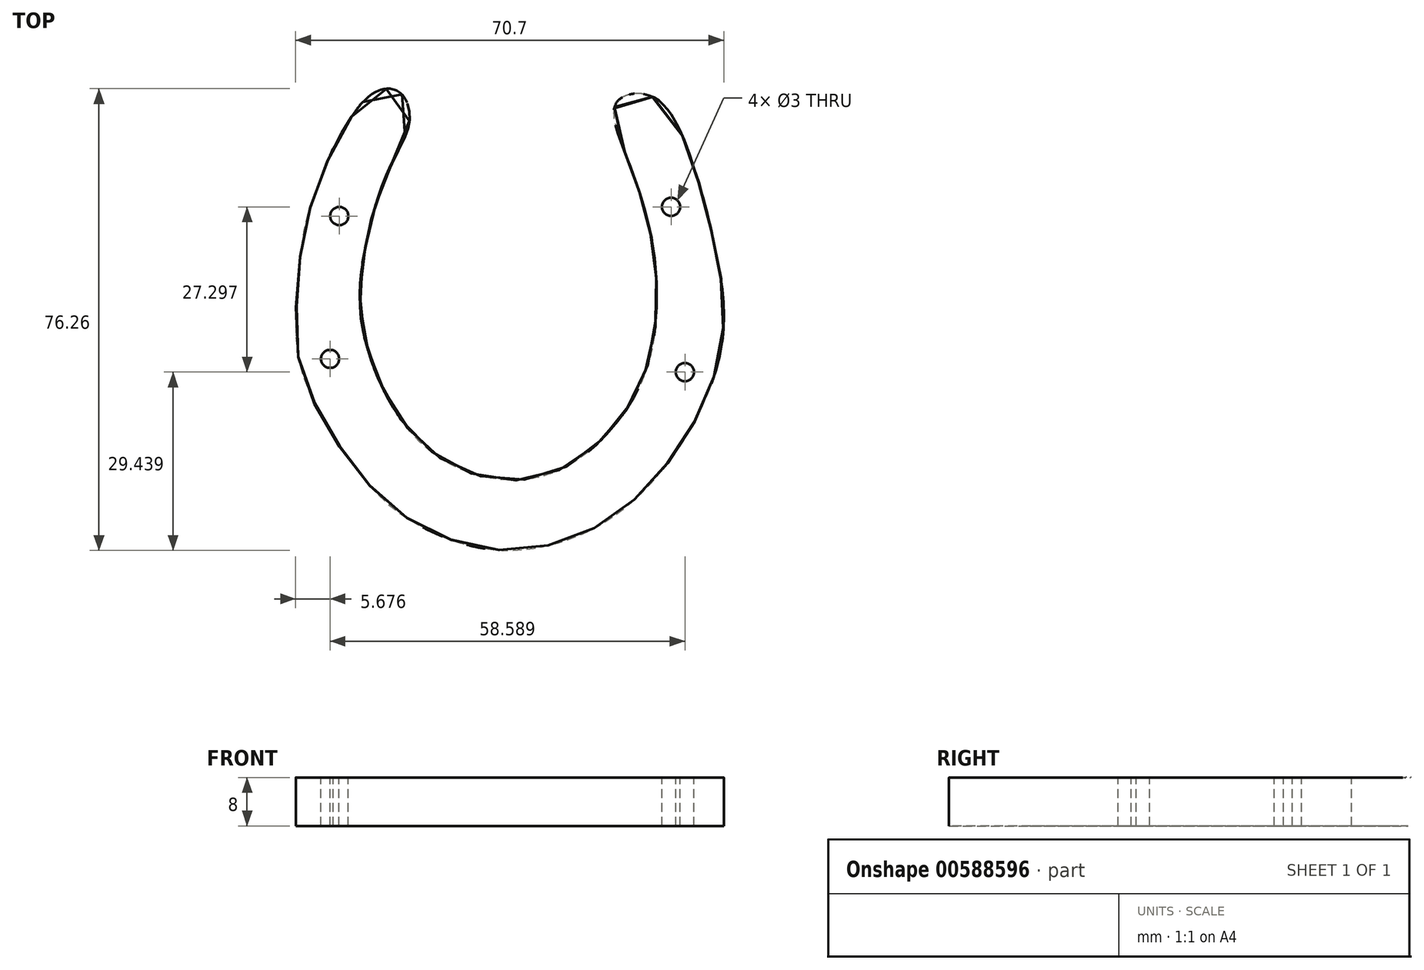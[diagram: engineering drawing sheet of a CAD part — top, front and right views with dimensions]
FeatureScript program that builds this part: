
annotation { "Feature Type Name" : "Feature", "Feature Type Description" : "" }
export const myFeature = defineFeature(function(context is Context, id is Id, definition is map)
    precondition{}
    {
        {
            var Q0;
            Q0=qCreatedBy(makeId("Top.planeOp"),FACE);
            var sketch = newSketch(context, id + "F0", { "sketchPlane" : qUnion([Q0])});
            skFitSpline(sketch, "E0", {"points": [v(-64.34, 65.8) * mm, v(-67.4, 58.26) * mm, v(-69.55, 49.73) * mm, v(-70.25, 41.3) * mm, v(-70.25, 32.14) * mm, v(-66.74, 22.35) * mm, v(-60.76, 13.17) * mm, v(-53.93, 5.9) * mm, v(-41.12, 0) * mm, v(-29.59, 0) * mm, v(-17.63, 5.26) * mm, v(-5.96, 18.33) * mm, v(0, 34.6) * mm, v(-1.2, 49.14) * mm, v(-5.1, 63.6) * mm, v(-11.57, 74.25) * mm, v(-17.47, 73.4) * mm, v(-17, 67.31) * mm, v(-13.66, 58.27) * mm, v(-11.29, 47.81) * mm, v(-11.1, 36.87) * mm, v(-13.85, 26.22) * mm, v(-23.94, 14.33) * mm, v(-36.2, 11) * mm, v(-50.19, 17.47) * mm, v(-59.32, 35.26) * mm, v(-59.22, 48.2) * mm, v(-55.23, 62.08) * mm, v(-51.7, 70.35) * mm, v(-53.52, 75.1) * mm, v(-59.32, 73.5) * mm, v(-64.83, 64.55) * mm, v(-64.34, 65.8) * mm]});
            skSolve(sketch);
        }
        {
            var Q0;
            Q0 = qSketchRegion(id + "F0", true);
            extrude(context, id + "F1", {"entities" : qUnion([Q0]), "depth" : 8 * mm, "offsetDistance" : 25 * mm});
        }
        {
            var Q0;
            Q0=makeQuery(id+"F1.opExtrude","CAP_FACE",FACE,{"disambiguationData":[OSD([sQuery(id+"F0.wireOp",EDGE,"E0")])],"isStart":false});
            var sketch = newSketch(context, id + "F2", { "sketchPlane" : qUnion([Q0])});
            skPoint(sketch, "E1", {"position": v(-63.31, 54.56) * mm});
            skPoint(sketch, "E2", {"position": v(-65.6, 34.12) * mm});
            skPoint(sketch, "E3", {"position": v(-60.08, 18.8) * mm});
            skPoint(sketch, "E4", {"position": v(-12.71, 16.62) * mm});
            skPoint(sketch, "E5", {"position": v(-9.2, 56.94) * mm});
            skPoint(sketch, "E6", {"position": v(-5.96, 35.54) * mm});
            skSolve(sketch);
        }
        {
            var Q0;
            Q0=sQuery(id+"F2.wireOp",VERTEX,"E1");
            var Q1;
            Q1=makeQuery(id+"F1.opExtrude","SWEPT_BODY",BODY,{"disambiguationData":[OSD([sQuery(id+"F0.wireOp",EDGE,"E0")])]});
            hole(context, id + "F3", {"style" : HoleStyle.SIMPLE, "endStyle" : HoleEndStyle.THROUGH, "holeDiameter" : 3 * mm, "majorDiameter" : 5 * mm, "isTappedThrough" : true, "tappedDepth" : 12 * mm, "tapClearance" : 3, "locations" : qUnion([Q0]), "scope" : qUnion([Q1])});
        }
        {
            var Q0;
            Q0=makeQuery(id+"F1.opExtrude","CAP_FACE",FACE,{"disambiguationData":[OSD([sQuery(id+"F0.wireOp",EDGE,"E0")])],"isStart":false});
            var sketch = newSketch(context, id + "F4", { "sketchPlane" : qUnion([Q0])});
            skPoint(sketch, "E7", {"position": v(-64.83, 30.98) * mm});
            skSolve(sketch);
        }
        {
            var Q0;
            Q0=sQuery(id+"F4.wireOp",VERTEX,"E7");
            var Q1;
            Q1=makeQuery(id+"F1.opExtrude","SWEPT_BODY",BODY,{"disambiguationData":[OSD([sQuery(id+"F0.wireOp",EDGE,"E0")])]});
            hole(context, id + "F5", {"style" : HoleStyle.SIMPLE, "endStyle" : HoleEndStyle.THROUGH, "holeDiameter" : 3 * mm, "majorDiameter" : 5 * mm, "isTappedThrough" : true, "tappedDepth" : 12 * mm, "tapClearance" : 3, "locations" : qUnion([Q0]), "scope" : qUnion([Q1])});
        }
        {
            var Q0;
            Q0=makeQuery(id+"F1.opExtrude","CAP_FACE",FACE,{"disambiguationData":[OSD([sQuery(id+"F0.wireOp",EDGE,"E0")])],"isStart":false});
            var sketch = newSketch(context, id + "F6", { "sketchPlane" : qUnion([Q0])});
            skPoint(sketch, "E8", {"position": v(-8.53, 56.09) * mm});
            skSolve(sketch);
        }
        {
            var Q0;
            Q0=sQuery(id+"F6.wireOp",VERTEX,"E8");
            var Q1;
            Q1=makeQuery(id+"F1.opExtrude","SWEPT_BODY",BODY,{"disambiguationData":[OSD([sQuery(id+"F0.wireOp",EDGE,"E0")])]});
            hole(context, id + "F7", {"style" : HoleStyle.SIMPLE, "endStyle" : HoleEndStyle.THROUGH, "holeDiameter" : 3 * mm, "majorDiameter" : 5 * mm, "isTappedThrough" : true, "tappedDepth" : 12 * mm, "tapClearance" : 3, "locations" : qUnion([Q0]), "scope" : qUnion([Q1])});
        }
        {
            var Q0;
            Q0=makeQuery(id+"F1.opExtrude","CAP_FACE",FACE,{"disambiguationData":[OSD([sQuery(id+"F0.wireOp",EDGE,"E0")])],"isStart":false});
            var sketch = newSketch(context, id + "F8", { "sketchPlane" : qUnion([Q0])});
            skPoint(sketch, "E9", {"position": v(-6.24, 28.79) * mm});
            skSolve(sketch);
        }
        {
            var Q0;
            Q0=sQuery(id+"F8.wireOp",VERTEX,"E9");
            var Q1;
            Q1=makeQuery(id+"F1.opExtrude","SWEPT_BODY",BODY,{"disambiguationData":[OSD([sQuery(id+"F0.wireOp",EDGE,"E0")])]});
            hole(context, id + "F9", {"style" : HoleStyle.SIMPLE, "endStyle" : HoleEndStyle.THROUGH, "holeDiameter" : 3 * mm, "majorDiameter" : 5 * mm, "isTappedThrough" : true, "tappedDepth" : 12 * mm, "tapClearance" : 3, "locations" : qUnion([Q0]), "scope" : qUnion([Q1])});
        }
        {
            var Q0;
            Q0=makeQuery(id+"F1.opExtrude","CAP_FACE",FACE,{"disambiguationData":[OSD([sQuery(id+"F0.wireOp",EDGE,"E0")])],"isStart":false});
            fillet(context, id + "F10", {"entities" : qUnion([Q0]), "radius" : 0.02 * mm, "tangentPropagation" : true, "allowEdgeOverflow" : false});
        }
    });
